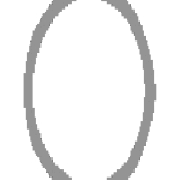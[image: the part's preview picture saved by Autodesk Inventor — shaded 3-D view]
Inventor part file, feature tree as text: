
AUTODESK INVENTOR PART (.ipt)
format: ipt  version: 2021 (Build 250183000, 183)  size: 161,792 bytes
history: native  units: in
note: dims shown in document units (in); Inventor stores cm internally (conversion verified against a paired STEP export)
features: other x5, sketch x2, sweep x1, plane x1
ambient origin geometry x8: Origin, YZ Plane, XZ Plane, XY Plane, X Axis, Y Axis, Z Axis, Center Point
bodies: Solid1 (feature_tree), Body (feature_tree)
feature tree (9):
  other  "Driven Length"
  other  "Frame Generator"
  other  "Start Plane"
  other  "End Plane"
  sweep  "Sweep Path"
  other  "Orientation Work Plane"
  sketch  "Sketch2"  dims[d0=1.0in d1=0.065in]
  plane  "Work Plane3"
  sketch  "Sketch3"  dims[d2=7.854in d4=-0.0in d5=7.854in d8=90.0deg d9=7.854in d10=0.0in d11=0.0in]
